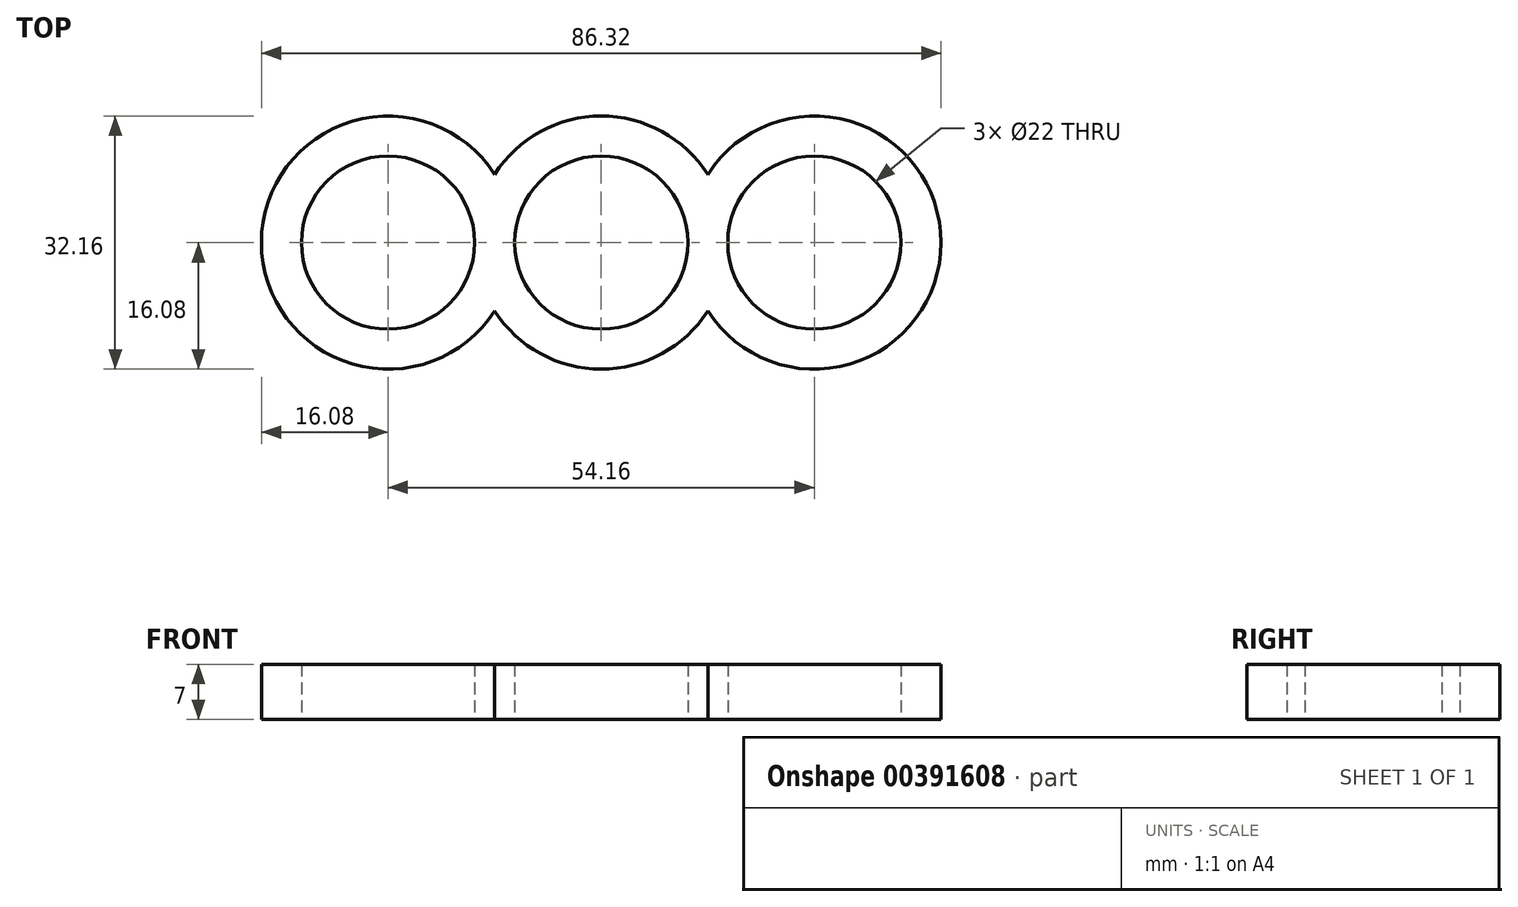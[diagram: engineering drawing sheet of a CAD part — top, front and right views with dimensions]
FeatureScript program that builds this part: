
annotation { "Feature Type Name" : "Feature", "Feature Type Description" : "" }
export const myFeature = defineFeature(function(context is Context, id is Id, definition is map)
    precondition{}
    {
        {
            var Q0;
            Q0=qCreatedBy(makeId("Top.planeOp"),FACE);
            var sketch = newSketch(context, id + "F0", { "sketchPlane" : qUnion([Q0])});
            skArc(sketch, "E0", {"start": v(0, 11) * mm, "mid": v(-11, 0) * mm, "end": v(0, -11) * mm});
            skCircle(sketch, "E1", {"center": v(-27.08, 0) * mm, "radius": 11 * mm});
            skPoint(sketch, "E2.orphan", {"position": v(-43.16, 16.08) * mm});
            skPoint(sketch, "E3.orphan", {"position": v(-43.16, -16.08) * mm});
            skPoint(sketch, "E4.start.orphan", {"position": v(-43.16, 0) * mm});
            skArc(sketch, "E5", {"start": v(-27.08, -16.08) * mm, "mid": v(-43.16, 0) * mm, "end": v(-27.08, 16.08) * mm});
            skArc(sketch, "E6", {"start": v(-27.08, 16.08) * mm, "mid": v(-19.36, 14.1) * mm, "end": v(-13.54, 8.67) * mm});
            skArc(sketch, "E7", {"start": v(0, 16.08) * mm, "mid": v(-7.72, 14.1) * mm, "end": v(-13.54, 8.67) * mm});
            skPoint(sketch, "E8.orphan", {"position": v(-16.08, 0) * mm});
            skPoint(sketch, "E9.orphan", {"position": v(-11, 0) * mm});
            skArc(sketch, "E10", {"start": v(-27.08, -16.08) * mm, "mid": v(-19.36, -14.1) * mm, "end": v(-13.54, -8.67) * mm});
            skArc(sketch, "E11", {"start": v(0, -16.08) * mm, "mid": v(-7.72, -14.1) * mm, "end": v(-13.54, -8.67) * mm});
            skCircle(sketch, "E12.MirrorC", {"center": v(27.08, 0) * mm, "radius": 11 * mm});
            skPoint(sketch, "E13.MirrorP", {"position": v(11, 0) * mm});
            skPoint(sketch, "E14.MirrorP", {"position": v(16.08, 0) * mm});
            skPoint(sketch, "E15.MirrorP", {"position": v(43.16, 16.08) * mm});
            skArc(sketch, "E16.MirrorCS", {"start": v(27.08, -16.08) * mm, "mid": v(43.16, 0) * mm, "end": v(27.08, 16.08) * mm});
            skArc(sketch, "E17.MirrorCS", {"start": v(0, 16.08) * mm, "mid": v(7.72, 14.1) * mm, "end": v(13.54, 8.67) * mm});
            skArc(sketch, "E18.MirrorCS", {"start": v(0, 11) * mm, "mid": v(11, 0) * mm, "end": v(0, -11) * mm});
            skArc(sketch, "E19.MirrorCS", {"start": v(27.08, 16.08) * mm, "mid": v(19.36, 14.1) * mm, "end": v(13.54, 8.67) * mm});
            skArc(sketch, "E20.MirrorCS", {"start": v(27.08, -16.08) * mm, "mid": v(19.36, -14.1) * mm, "end": v(13.54, -8.67) * mm});
            skPoint(sketch, "E21.MirrorP", {"position": v(43.16, 0) * mm});
            skArc(sketch, "E22.MirrorCS", {"start": v(0, -16.08) * mm, "mid": v(7.72, -14.1) * mm, "end": v(13.54, -8.67) * mm});
            skPoint(sketch, "E23.MirrorP", {"position": v(43.16, -16.08) * mm});
            skSolve(sketch);
        }
        {
            var Q0;
            Q0 = qSketchRegion(id + "F0", true);
            extrude(context, id + "F1", {"entities" : qUnion([Q0]), "depth" : 7 * mm});
        }
    });
